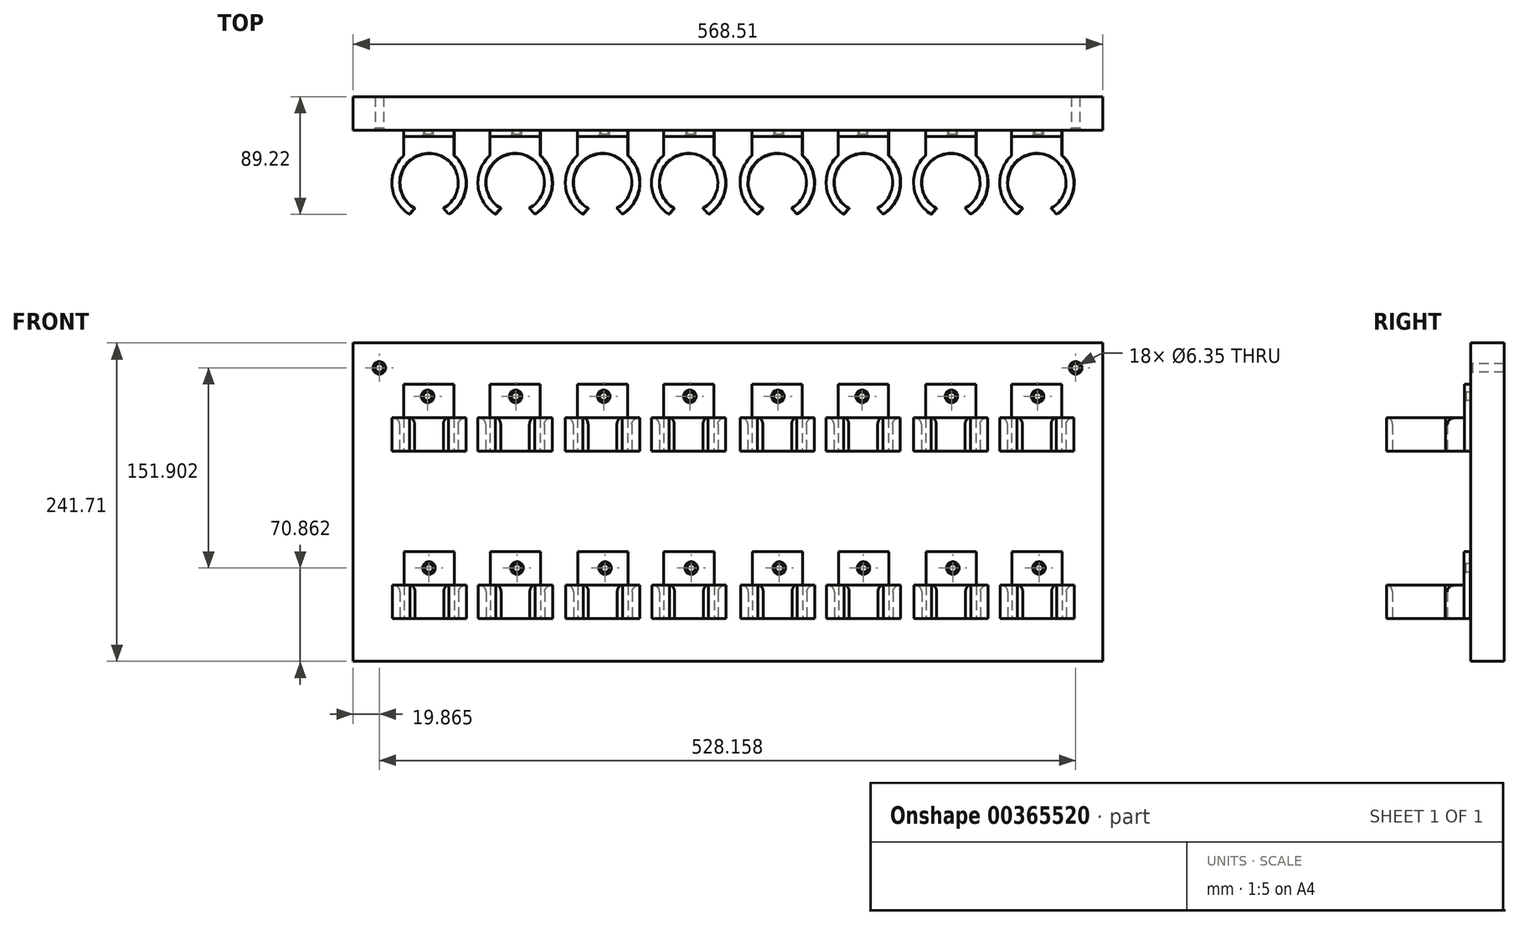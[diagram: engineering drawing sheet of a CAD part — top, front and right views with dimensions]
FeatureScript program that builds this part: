
annotation { "Feature Type Name" : "Feature", "Feature Type Description" : "" }
export const myFeature = defineFeature(function(context is Context, id is Id, definition is map)
    precondition{}
    {
        {
            var Q0;
            Q0=qCreatedBy(makeId("Top.planeOp"),FACE);
            var sketch = newSketch(context, id + "F0", { "sketchPlane" : qUnion([Q0])});
            skLineSegment(sketch, "E0.bottom", {"start": v(-209.16, -7.42) * mm, "end": v(-171.02, -7.42) * mm});
            skLineSegment(sketch, "E0.left", {"start": v(-209.16, -7.42) * mm, "end": v(-209.16, -26.47) * mm});
            skLineSegment(sketch, "E0.right", {"start": v(-171.02, -7.42) * mm, "end": v(-171.02, -26.47) * mm});
            skArc(sketch, "E1", {"start": v(-209.16, -26.47) * mm, "mid": v(-218.1, -49.8) * mm, "end": v(-204.97, -71.04) * mm});
            skArc(sketch, "E2", {"start": v(-175.21, -71.04) * mm, "mid": v(-190.1, -19.02) * mm, "end": v(-204.97, -71.04) * mm});
            skArc(sketch, "E3", {"start": v(-179.16, -66.5) * mm, "mid": v(-190.1, -24.93) * mm, "end": v(-201.02, -66.5) * mm});
            skPoint(sketch, "E4", {"position": v(-201.02, -66.5) * mm});
            skPoint(sketch, "E5", {"position": v(-204.97, -71.04) * mm});
            skPoint(sketch, "E6.MirrorP", {"position": v(-179.16, -66.5) * mm});
            skPoint(sketch, "E7.MirrorP", {"position": v(-175.21, -71.04) * mm});
            skArc(sketch, "E8.trimOffspring", {"start": v(-175.21, -71.04) * mm, "mid": v(-162.08, -49.8) * mm, "end": v(-171.02, -26.47) * mm});
            skPoint(sketch, "E9.orphan", {"position": v(-190.1, -7.42) * mm});
            skLineSegment(sketch, "E10", {"start": v(-201.02, -66.5) * mm, "end": v(-204.97, -71.04) * mm});
            skLineSegment(sketch, "E11", {"start": v(-179.16, -66.5) * mm, "end": v(-175.21, -71.04) * mm});
            skLineSegment(sketch, "E12.left", {"start": v(-209.16, -7.42) * mm, "end": v(-209.16, -16.94) * mm});
            skLineSegment(sketch, "E12.right", {"start": v(-171.02, -7.42) * mm, "end": v(-171.02, -16.94) * mm});
            skPoint(sketch, "E13.end.orphan", {"position": v(-209.16, -12.18) * mm});
            skPoint(sketch, "E13.start.orphan", {"position": v(-171.02, -12.18) * mm});
            skLineSegment(sketch, "E14.bottom", {"start": v(-209.16, -12.18) * mm, "end": v(-171.02, -12.18) * mm});
            skLineSegment(sketch, "E14.left", {"start": v(-209.16, -12.18) * mm, "end": v(-209.16, -7.42) * mm});
            skLineSegment(sketch, "E14.right", {"start": v(-171.02, -12.18) * mm, "end": v(-171.02, -7.42) * mm});
            skPoint(sketch, "E14.top.end.orphan", {"position": v(-171.02, -2.68) * mm});
            skLineSegment(sketch, "E15.bottom", {"start": v(-274.44, -7.42) * mm, "end": v(-236.3, -7.42) * mm});
            skLineSegment(sketch, "E15.left", {"start": v(-274.44, -7.42) * mm, "end": v(-274.44, -26.47) * mm});
            skLineSegment(sketch, "E15.right", {"start": v(-236.3, -7.42) * mm, "end": v(-236.3, -26.47) * mm});
            skArc(sketch, "E16", {"start": v(-274.44, -26.47) * mm, "mid": v(-283.38, -49.8) * mm, "end": v(-270.25, -71.04) * mm});
            skArc(sketch, "E17", {"start": v(-240.5, -71.04) * mm, "mid": v(-255.37, -19.02) * mm, "end": v(-270.25, -71.04) * mm});
            skArc(sketch, "E18", {"start": v(-244.44, -66.5) * mm, "mid": v(-255.37, -24.93) * mm, "end": v(-266.3, -66.5) * mm});
            skPoint(sketch, "E19", {"position": v(-266.3, -66.5) * mm});
            skPoint(sketch, "E20", {"position": v(-270.25, -71.04) * mm});
            skPoint(sketch, "E21.MirrorP", {"position": v(-244.44, -66.5) * mm});
            skPoint(sketch, "E22.MirrorP", {"position": v(-240.5, -71.04) * mm});
            skArc(sketch, "E23.trimOffspring", {"start": v(-240.5, -71.04) * mm, "mid": v(-227.36, -49.8) * mm, "end": v(-236.3, -26.47) * mm});
            skPoint(sketch, "E24.orphan", {"position": v(-255.37, -7.42) * mm});
            skLineSegment(sketch, "E25", {"start": v(-266.3, -66.5) * mm, "end": v(-270.25, -71.04) * mm});
            skLineSegment(sketch, "E26", {"start": v(-244.44, -66.5) * mm, "end": v(-240.5, -71.04) * mm});
            skLineSegment(sketch, "E27.left", {"start": v(-274.44, -7.42) * mm, "end": v(-274.44, -16.94) * mm});
            skLineSegment(sketch, "E27.right", {"start": v(-236.3, -7.42) * mm, "end": v(-236.3, -16.94) * mm});
            skPoint(sketch, "E28.end.orphan", {"position": v(-274.44, -12.18) * mm});
            skPoint(sketch, "E28.start.orphan", {"position": v(-236.3, -12.18) * mm});
            skLineSegment(sketch, "E29.bottom", {"start": v(-274.44, -12.18) * mm, "end": v(-236.3, -12.18) * mm});
            skLineSegment(sketch, "E29.left", {"start": v(-274.44, -12.18) * mm, "end": v(-274.44, -7.42) * mm});
            skLineSegment(sketch, "E29.right", {"start": v(-236.3, -12.18) * mm, "end": v(-236.3, -7.42) * mm});
            skPoint(sketch, "E29.top.end.orphan", {"position": v(-236.3, -2.68) * mm});
            skLineSegment(sketch, "E30.bottom", {"start": v(-77.55, -7.42) * mm, "end": v(-39.41, -7.42) * mm});
            skLineSegment(sketch, "E30.left", {"start": v(-77.55, -7.42) * mm, "end": v(-77.55, -26.47) * mm});
            skLineSegment(sketch, "E30.right", {"start": v(-39.41, -7.42) * mm, "end": v(-39.41, -26.47) * mm});
            skArc(sketch, "E31", {"start": v(-77.55, -26.47) * mm, "mid": v(-86.5, -49.8) * mm, "end": v(-73.36, -71.04) * mm});
            skArc(sketch, "E32", {"start": v(-43.6, -71.04) * mm, "mid": v(-58.48, -19.02) * mm, "end": v(-73.36, -71.04) * mm});
            skArc(sketch, "E33", {"start": v(-47.56, -66.5) * mm, "mid": v(-58.48, -24.93) * mm, "end": v(-69.41, -66.5) * mm});
            skPoint(sketch, "E34", {"position": v(-69.41, -66.5) * mm});
            skPoint(sketch, "E35", {"position": v(-73.36, -71.04) * mm});
            skPoint(sketch, "E36.MirrorP", {"position": v(-47.56, -66.5) * mm});
            skPoint(sketch, "E37.MirrorP", {"position": v(-43.6, -71.04) * mm});
            skArc(sketch, "E38.trimOffspring", {"start": v(-43.6, -71.04) * mm, "mid": v(-30.47, -49.8) * mm, "end": v(-39.41, -26.47) * mm});
            skPoint(sketch, "E39.orphan", {"position": v(-58.48, -7.42) * mm});
            skLineSegment(sketch, "E40", {"start": v(-69.41, -66.5) * mm, "end": v(-73.36, -71.04) * mm});
            skLineSegment(sketch, "E41", {"start": v(-47.56, -66.5) * mm, "end": v(-43.6, -71.04) * mm});
            skLineSegment(sketch, "E42.left", {"start": v(-77.55, -7.42) * mm, "end": v(-77.55, -16.94) * mm});
            skLineSegment(sketch, "E42.right", {"start": v(-39.41, -7.42) * mm, "end": v(-39.41, -16.94) * mm});
            skPoint(sketch, "E43.end.orphan", {"position": v(-77.55, -12.18) * mm});
            skPoint(sketch, "E43.start.orphan", {"position": v(-39.41, -12.18) * mm});
            skLineSegment(sketch, "E44.bottom", {"start": v(-77.55, -12.18) * mm, "end": v(-39.41, -12.18) * mm});
            skLineSegment(sketch, "E44.left", {"start": v(-77.55, -12.18) * mm, "end": v(-77.55, -7.42) * mm});
            skLineSegment(sketch, "E44.right", {"start": v(-39.41, -12.18) * mm, "end": v(-39.41, -7.42) * mm});
            skLineSegment(sketch, "E45.bottom", {"start": v(-142.83, -7.42) * mm, "end": v(-104.7, -7.42) * mm});
            skLineSegment(sketch, "E45.left", {"start": v(-142.83, -7.42) * mm, "end": v(-142.83, -26.47) * mm});
            skLineSegment(sketch, "E45.right", {"start": v(-104.7, -7.42) * mm, "end": v(-104.7, -26.47) * mm});
            skArc(sketch, "E46", {"start": v(-142.83, -26.47) * mm, "mid": v(-151.77, -49.8) * mm, "end": v(-138.64, -71.04) * mm});
            skArc(sketch, "E47", {"start": v(-108.88, -71.04) * mm, "mid": v(-123.76, -19.02) * mm, "end": v(-138.64, -71.04) * mm});
            skArc(sketch, "E48", {"start": v(-112.83, -66.5) * mm, "mid": v(-123.76, -24.93) * mm, "end": v(-134.69, -66.5) * mm});
            skPoint(sketch, "E49", {"position": v(-134.69, -66.5) * mm});
            skPoint(sketch, "E50", {"position": v(-138.64, -71.04) * mm});
            skPoint(sketch, "E51.MirrorP", {"position": v(-112.83, -66.5) * mm});
            skPoint(sketch, "E52.MirrorP", {"position": v(-108.88, -71.04) * mm});
            skArc(sketch, "E53.trimOffspring", {"start": v(-108.88, -71.04) * mm, "mid": v(-95.75, -49.8) * mm, "end": v(-104.7, -26.47) * mm});
            skPoint(sketch, "E54.orphan", {"position": v(-123.76, -7.42) * mm});
            skLineSegment(sketch, "E55", {"start": v(-134.69, -66.5) * mm, "end": v(-138.64, -71.04) * mm});
            skLineSegment(sketch, "E56", {"start": v(-112.83, -66.5) * mm, "end": v(-108.88, -71.04) * mm});
            skLineSegment(sketch, "E57.left", {"start": v(-142.83, -7.42) * mm, "end": v(-142.83, -16.94) * mm});
            skLineSegment(sketch, "E57.right", {"start": v(-104.7, -7.42) * mm, "end": v(-104.7, -16.94) * mm});
            skPoint(sketch, "E58.end.orphan", {"position": v(-142.83, -12.18) * mm});
            skPoint(sketch, "E58.start.orphan", {"position": v(-104.7, -12.18) * mm});
            skLineSegment(sketch, "E59.bottom", {"start": v(-142.83, -12.18) * mm, "end": v(-104.7, -12.18) * mm});
            skLineSegment(sketch, "E59.left", {"start": v(-142.83, -12.18) * mm, "end": v(-142.83, -7.42) * mm});
            skLineSegment(sketch, "E59.right", {"start": v(-104.7, -12.18) * mm, "end": v(-104.7, -7.42) * mm});
            skLineSegment(sketch, "E60.bottom", {"start": v(54.94, -7.42) * mm, "end": v(93.08, -7.42) * mm});
            skLineSegment(sketch, "E60.left", {"start": v(54.94, -7.42) * mm, "end": v(54.94, -26.47) * mm});
            skLineSegment(sketch, "E60.right", {"start": v(93.08, -7.42) * mm, "end": v(93.08, -26.47) * mm});
            skArc(sketch, "E61", {"start": v(54.94, -26.47) * mm, "mid": v(46, -49.8) * mm, "end": v(59.14, -71.04) * mm});
            skArc(sketch, "E62", {"start": v(88.89, -71.04) * mm, "mid": v(74.01, -19.02) * mm, "end": v(59.14, -71.04) * mm});
            skArc(sketch, "E63", {"start": v(84.94, -66.5) * mm, "mid": v(74.01, -24.93) * mm, "end": v(63.09, -66.5) * mm});
            skPoint(sketch, "E64", {"position": v(63.09, -66.5) * mm});
            skPoint(sketch, "E65", {"position": v(59.14, -71.04) * mm});
            skPoint(sketch, "E66.MirrorP", {"position": v(84.94, -66.5) * mm});
            skPoint(sketch, "E67.MirrorP", {"position": v(88.89, -71.04) * mm});
            skArc(sketch, "E68.trimOffspring", {"start": v(88.89, -71.04) * mm, "mid": v(102.03, -49.8) * mm, "end": v(93.08, -26.47) * mm});
            skPoint(sketch, "E69.orphan", {"position": v(74.01, -7.42) * mm});
            skLineSegment(sketch, "E70", {"start": v(63.09, -66.5) * mm, "end": v(59.14, -71.04) * mm});
            skLineSegment(sketch, "E71", {"start": v(84.94, -66.5) * mm, "end": v(88.89, -71.04) * mm});
            skLineSegment(sketch, "E72.left", {"start": v(54.94, -7.42) * mm, "end": v(54.94, -16.94) * mm});
            skLineSegment(sketch, "E72.right", {"start": v(93.08, -7.42) * mm, "end": v(93.08, -16.94) * mm});
            skPoint(sketch, "E73.end.orphan", {"position": v(54.94, -12.18) * mm});
            skPoint(sketch, "E73.start.orphan", {"position": v(93.08, -12.18) * mm});
            skLineSegment(sketch, "E74.bottom", {"start": v(54.94, -12.18) * mm, "end": v(93.08, -12.18) * mm});
            skLineSegment(sketch, "E74.left", {"start": v(54.94, -12.18) * mm, "end": v(54.94, -7.42) * mm});
            skLineSegment(sketch, "E74.right", {"start": v(93.08, -12.18) * mm, "end": v(93.08, -7.42) * mm});
            skPoint(sketch, "E74.top.end.orphan", {"position": v(93.08, -2.68) * mm});
            skLineSegment(sketch, "E75.bottom", {"start": v(-10.34, -7.42) * mm, "end": v(27.8, -7.42) * mm});
            skLineSegment(sketch, "E75.left", {"start": v(-10.34, -7.42) * mm, "end": v(-10.34, -26.47) * mm});
            skLineSegment(sketch, "E75.right", {"start": v(27.8, -7.42) * mm, "end": v(27.8, -26.47) * mm});
            skArc(sketch, "E76", {"start": v(-10.34, -26.47) * mm, "mid": v(-19.28, -49.8) * mm, "end": v(-6.14, -71.04) * mm});
            skArc(sketch, "E77", {"start": v(23.61, -71.04) * mm, "mid": v(8.73, -19.02) * mm, "end": v(-6.14, -71.04) * mm});
            skArc(sketch, "E78", {"start": v(19.66, -66.5) * mm, "mid": v(8.73, -24.93) * mm, "end": v(-2.2, -66.5) * mm});
            skPoint(sketch, "E79", {"position": v(-2.2, -66.5) * mm});
            skPoint(sketch, "E80", {"position": v(-6.14, -71.04) * mm});
            skPoint(sketch, "E81.MirrorP", {"position": v(19.66, -66.5) * mm});
            skPoint(sketch, "E82.MirrorP", {"position": v(23.61, -71.04) * mm});
            skArc(sketch, "E83.trimOffspring", {"start": v(23.61, -71.04) * mm, "mid": v(36.75, -49.8) * mm, "end": v(27.8, -26.47) * mm});
            skPoint(sketch, "E84.orphan", {"position": v(8.73, -7.42) * mm});
            skLineSegment(sketch, "E85", {"start": v(-2.2, -66.5) * mm, "end": v(-6.14, -71.04) * mm});
            skLineSegment(sketch, "E86", {"start": v(19.66, -66.5) * mm, "end": v(23.61, -71.04) * mm});
            skLineSegment(sketch, "E87.left", {"start": v(-10.34, -7.42) * mm, "end": v(-10.34, -16.94) * mm});
            skLineSegment(sketch, "E87.right", {"start": v(27.8, -7.42) * mm, "end": v(27.8, -16.94) * mm});
            skPoint(sketch, "E88.end.orphan", {"position": v(-10.34, -12.18) * mm});
            skPoint(sketch, "E88.start.orphan", {"position": v(27.8, -12.18) * mm});
            skLineSegment(sketch, "E89.bottom", {"start": v(-10.34, -12.18) * mm, "end": v(27.8, -12.18) * mm});
            skLineSegment(sketch, "E89.left", {"start": v(-10.34, -12.18) * mm, "end": v(-10.34, -7.42) * mm});
            skLineSegment(sketch, "E89.right", {"start": v(27.8, -12.18) * mm, "end": v(27.8, -7.42) * mm});
            skPoint(sketch, "E89.top.end.orphan", {"position": v(27.8, -2.68) * mm});
            skLineSegment(sketch, "E90.bottom", {"start": v(186.55, -7.42) * mm, "end": v(224.7, -7.42) * mm});
            skLineSegment(sketch, "E90.left", {"start": v(186.55, -7.42) * mm, "end": v(186.55, -26.47) * mm});
            skLineSegment(sketch, "E90.right", {"start": v(224.7, -7.42) * mm, "end": v(224.7, -26.47) * mm});
            skArc(sketch, "E91", {"start": v(186.55, -26.47) * mm, "mid": v(177.6, -49.8) * mm, "end": v(190.74, -71.04) * mm});
            skArc(sketch, "E92", {"start": v(220.5, -71.04) * mm, "mid": v(205.62, -19.02) * mm, "end": v(190.74, -71.04) * mm});
            skArc(sketch, "E93", {"start": v(216.55, -66.5) * mm, "mid": v(205.62, -24.93) * mm, "end": v(194.7, -66.5) * mm});
            skPoint(sketch, "E94", {"position": v(194.7, -66.5) * mm});
            skPoint(sketch, "E95", {"position": v(190.74, -71.04) * mm});
            skPoint(sketch, "E96.MirrorP", {"position": v(216.55, -66.5) * mm});
            skPoint(sketch, "E97.MirrorP", {"position": v(220.5, -71.04) * mm});
            skArc(sketch, "E98.trimOffspring", {"start": v(220.5, -71.04) * mm, "mid": v(233.63, -49.8) * mm, "end": v(224.7, -26.47) * mm});
            skPoint(sketch, "E99.orphan", {"position": v(205.62, -7.42) * mm});
            skLineSegment(sketch, "E100", {"start": v(194.7, -66.5) * mm, "end": v(190.74, -71.04) * mm});
            skLineSegment(sketch, "E101", {"start": v(216.55, -66.5) * mm, "end": v(220.5, -71.04) * mm});
            skLineSegment(sketch, "E102.left", {"start": v(186.55, -7.42) * mm, "end": v(186.55, -16.94) * mm});
            skLineSegment(sketch, "E102.right", {"start": v(224.7, -7.42) * mm, "end": v(224.7, -16.94) * mm});
            skPoint(sketch, "E103.end.orphan", {"position": v(186.55, -12.18) * mm});
            skPoint(sketch, "E103.start.orphan", {"position": v(224.7, -12.18) * mm});
            skLineSegment(sketch, "E104.bottom", {"start": v(186.55, -12.18) * mm, "end": v(224.7, -12.18) * mm});
            skLineSegment(sketch, "E104.left", {"start": v(186.55, -12.18) * mm, "end": v(186.55, -7.42) * mm});
            skLineSegment(sketch, "E104.right", {"start": v(224.7, -12.18) * mm, "end": v(224.7, -7.42) * mm});
            skLineSegment(sketch, "E105.bottom", {"start": v(121.27, -7.42) * mm, "end": v(159.41, -7.42) * mm});
            skLineSegment(sketch, "E105.left", {"start": v(121.27, -7.42) * mm, "end": v(121.27, -26.47) * mm});
            skLineSegment(sketch, "E105.right", {"start": v(159.41, -7.42) * mm, "end": v(159.41, -26.47) * mm});
            skArc(sketch, "E106", {"start": v(121.27, -26.47) * mm, "mid": v(112.33, -49.8) * mm, "end": v(125.47, -71.04) * mm});
            skArc(sketch, "E107", {"start": v(155.22, -71.04) * mm, "mid": v(140.34, -19.02) * mm, "end": v(125.47, -71.04) * mm});
            skArc(sketch, "E108", {"start": v(151.27, -66.5) * mm, "mid": v(140.34, -24.93) * mm, "end": v(129.42, -66.5) * mm});
            skPoint(sketch, "E109", {"position": v(129.42, -66.5) * mm});
            skPoint(sketch, "E110", {"position": v(125.47, -71.04) * mm});
            skPoint(sketch, "E111.MirrorP", {"position": v(151.27, -66.5) * mm});
            skPoint(sketch, "E112.MirrorP", {"position": v(155.22, -71.04) * mm});
            skArc(sketch, "E113.trimOffspring", {"start": v(155.22, -71.04) * mm, "mid": v(168.36, -49.8) * mm, "end": v(159.41, -26.47) * mm});
            skPoint(sketch, "E114.orphan", {"position": v(140.34, -7.42) * mm});
            skLineSegment(sketch, "E115", {"start": v(129.42, -66.5) * mm, "end": v(125.47, -71.04) * mm});
            skLineSegment(sketch, "E116", {"start": v(151.27, -66.5) * mm, "end": v(155.22, -71.04) * mm});
            skLineSegment(sketch, "E117.left", {"start": v(121.27, -7.42) * mm, "end": v(121.27, -16.94) * mm});
            skLineSegment(sketch, "E117.right", {"start": v(159.41, -7.42) * mm, "end": v(159.41, -16.94) * mm});
            skPoint(sketch, "E118.end.orphan", {"position": v(121.27, -12.18) * mm});
            skPoint(sketch, "E118.start.orphan", {"position": v(159.41, -12.18) * mm});
            skLineSegment(sketch, "E119.bottom", {"start": v(121.27, -12.18) * mm, "end": v(159.41, -12.18) * mm});
            skLineSegment(sketch, "E119.left", {"start": v(121.27, -12.18) * mm, "end": v(121.27, -7.42) * mm});
            skLineSegment(sketch, "E119.right", {"start": v(159.41, -12.18) * mm, "end": v(159.41, -7.42) * mm});
            skSolve(sketch);
        }
        {
            var Q0;
            {var subQ1=sQuery(id+"F0.wireOp",EDGE,"E15.left");Q0=makeQuery(id+"F0.imprint","IMPRINT",FACE,{"disambiguationData":[TD([[makeQuery(id+"F0.imprint","IMPRINT",EDGE,{"derivedFrom":subQ1}),1.0]])]});}
            var Q1;
            Q1=makeQuery(id+"F0.imprint","IMPRINT",FACE,{"disambiguationData":[TD([[makeQuery(id+"F0.imprint","IMPRINT",EDGE,{"derivedFrom":sQuery(id+"F0.wireOp",EDGE,"E18")}),-1.0]])]});
            var Q2;
            Q2=makeQuery(id+"F0.imprint","IMPRINT",FACE,{"disambiguationData":[TD([[makeQuery(id+"F0.imprint","IMPRINT",EDGE,{"derivedFrom":sQuery(id+"F0.wireOp",EDGE,"E3")}),-1.0]])]});
            var Q3;
            {var subQ1=sQuery(id+"F0.wireOp",EDGE,"E0.left");Q3=makeQuery(id+"F0.imprint","IMPRINT",FACE,{"disambiguationData":[TD([[makeQuery(id+"F0.imprint","IMPRINT",EDGE,{"derivedFrom":subQ1}),1.0]])]});}
            var Q4;
            {var subQ1=sQuery(id+"F0.wireOp",EDGE,"E45.left");Q4=makeQuery(id+"F0.imprint","IMPRINT",FACE,{"disambiguationData":[TD([[makeQuery(id+"F0.imprint","IMPRINT",EDGE,{"derivedFrom":subQ1}),1.0]])]});}
            var Q5;
            Q5=makeQuery(id+"F0.imprint","IMPRINT",FACE,{"disambiguationData":[TD([[makeQuery(id+"F0.imprint","IMPRINT",EDGE,{"derivedFrom":sQuery(id+"F0.wireOp",EDGE,"E48")}),-1.0]])]});
            var Q6;
            Q6=makeQuery(id+"F0.imprint","IMPRINT",FACE,{"disambiguationData":[TD([[makeQuery(id+"F0.imprint","IMPRINT",EDGE,{"derivedFrom":sQuery(id+"F0.wireOp",EDGE,"E33")}),-1.0]])]});
            var Q7;
            Q7=makeQuery(id+"F0.imprint","IMPRINT",FACE,{"disambiguationData":[TD([[makeQuery(id+"F0.imprint","IMPRINT",EDGE,{"derivedFrom":sQuery(id+"F0.wireOp",EDGE,"E78")}),-1.0]])]});
            var Q8;
            Q8=makeQuery(id+"F0.imprint","IMPRINT",FACE,{"disambiguationData":[TD([[makeQuery(id+"F0.imprint","IMPRINT",EDGE,{"derivedFrom":sQuery(id+"F0.wireOp",EDGE,"E63")}),-1.0]])]});
            var Q9;
            Q9=makeQuery(id+"F0.imprint","IMPRINT",FACE,{"disambiguationData":[TD([[makeQuery(id+"F0.imprint","IMPRINT",EDGE,{"derivedFrom":sQuery(id+"F0.wireOp",EDGE,"E108")}),-1.0]])]});
            var Q10;
            Q10=makeQuery(id+"F0.imprint","IMPRINT",FACE,{"disambiguationData":[TD([[makeQuery(id+"F0.imprint","IMPRINT",EDGE,{"derivedFrom":sQuery(id+"F0.wireOp",EDGE,"E93")}),-1.0]])]});
            var Q11;
            {var subQ1=sQuery(id+"F0.wireOp",EDGE,"E105.left");Q11=makeQuery(id+"F0.imprint","IMPRINT",FACE,{"disambiguationData":[TD([[makeQuery(id+"F0.imprint","IMPRINT",EDGE,{"derivedFrom":subQ1}),1.0]])]});}
            var Q12;
            {var subQ1=sQuery(id+"F0.wireOp",EDGE,"E60.left");Q12=makeQuery(id+"F0.imprint","IMPRINT",FACE,{"disambiguationData":[TD([[makeQuery(id+"F0.imprint","IMPRINT",EDGE,{"derivedFrom":subQ1}),1.0]])]});}
            var Q13;
            {var subQ1=sQuery(id+"F0.wireOp",EDGE,"E75.left");Q13=makeQuery(id+"F0.imprint","IMPRINT",FACE,{"disambiguationData":[TD([[makeQuery(id+"F0.imprint","IMPRINT",EDGE,{"derivedFrom":subQ1}),1.0]])]});}
            var Q14;
            {var subQ1=sQuery(id+"F0.wireOp",EDGE,"E30.left");Q14=makeQuery(id+"F0.imprint","IMPRINT",FACE,{"disambiguationData":[TD([[makeQuery(id+"F0.imprint","IMPRINT",EDGE,{"derivedFrom":subQ1}),1.0]])]});}
            var Q15;
            {var subQ1=sQuery(id+"F0.wireOp",EDGE,"E90.left");Q15=makeQuery(id+"F0.imprint","IMPRINT",FACE,{"disambiguationData":[TD([[makeQuery(id+"F0.imprint","IMPRINT",EDGE,{"derivedFrom":subQ1}),1.0]])]});}
            var Q16;
            Q16=makeQuery(id+"F0.imprint","IMPRINT",FACE,{"disambiguationData":[TD([[makeQuery(id+"F0.imprint","IMPRINT",EDGE,{"derivedFrom":sQuery(id+"F0.wireOp",EDGE,"c035edba-2ca9-43be-b41b-8822a2fe950e")}),-1.0]])]});
            var Q17;
            {var subQ1=sQuery(id+"F0.wireOp",EDGE,"01a7d978-39eb-4d9a-a90e-11414904825e.left");Q17=makeQuery(id+"F0.imprint","IMPRINT",FACE,{"disambiguationData":[TD([[makeQuery(id+"F0.imprint","IMPRINT",EDGE,{"derivedFrom":subQ1}),1.0]])]});}
            extrude(context, id + "F1", {"entities" : qUnion([Q0, Q1, Q2, Q3, Q4, Q5, Q6, Q7, Q8, Q9, Q10, Q11, Q12, Q13, Q14, Q15, Q16, Q17]), "depth" : 25.4 * mm});
        }
        {
            var Q0;
            Q0=qCreatedBy(makeId("Top.planeOp"),FACE);
            cPlane(context, id + "F2", {"entities" : qUnion([Q0]), "cplaneType" : CPlaneType.OFFSET, "offset" : 127 * mm, "oppositeDirection" : true, "width" : 152.4 * mm, "height" : 152.4 * mm});
        }
        {
            var Q0;
            Q0=qCreatedBy(id+"F2.planeOp",FACE);
            var sketch = newSketch(context, id + "F3", { "sketchPlane" : qUnion([Q0])});
            skLineSegment(sketch, "E120.bottom", {"start": v(-208.88, -7.62) * mm, "end": v(-170.73, -7.62) * mm});
            skLineSegment(sketch, "E120.left", {"start": v(-208.88, -7.62) * mm, "end": v(-208.88, -26.67) * mm});
            skLineSegment(sketch, "E120.right", {"start": v(-170.73, -7.62) * mm, "end": v(-170.73, -26.67) * mm});
            skArc(sketch, "E121", {"start": v(-208.88, -26.67) * mm, "mid": v(-217.82, -50) * mm, "end": v(-204.68, -71.24) * mm});
            skArc(sketch, "E122", {"start": v(-174.93, -71.24) * mm, "mid": v(-189.8, -19.22) * mm, "end": v(-204.68, -71.24) * mm});
            skArc(sketch, "E123", {"start": v(-178.88, -66.7) * mm, "mid": v(-189.8, -25.13) * mm, "end": v(-200.73, -66.7) * mm});
            skPoint(sketch, "E124", {"position": v(-200.73, -66.7) * mm});
            skPoint(sketch, "E125", {"position": v(-204.68, -71.24) * mm});
            skPoint(sketch, "E126.MirrorP", {"position": v(-178.88, -66.7) * mm});
            skPoint(sketch, "E127.MirrorP", {"position": v(-174.93, -71.24) * mm});
            skArc(sketch, "E128.trimOffspring", {"start": v(-174.93, -71.24) * mm, "mid": v(-161.8, -50) * mm, "end": v(-170.73, -26.67) * mm});
            skPoint(sketch, "E129.orphan", {"position": v(-189.8, -7.62) * mm});
            skLineSegment(sketch, "E130", {"start": v(-200.73, -66.7) * mm, "end": v(-204.68, -71.24) * mm});
            skLineSegment(sketch, "E131", {"start": v(-178.88, -66.7) * mm, "end": v(-174.93, -71.24) * mm});
            skLineSegment(sketch, "E132.left", {"start": v(-208.88, -7.62) * mm, "end": v(-208.88, -17.14) * mm});
            skLineSegment(sketch, "E132.right", {"start": v(-170.73, -7.62) * mm, "end": v(-170.73, -17.14) * mm});
            skPoint(sketch, "E133.end.orphan", {"position": v(-208.88, -12.38) * mm});
            skPoint(sketch, "E133.start.orphan", {"position": v(-170.73, -12.38) * mm});
            skLineSegment(sketch, "E134.bottom", {"start": v(-208.88, -12.38) * mm, "end": v(-170.73, -12.38) * mm});
            skLineSegment(sketch, "E134.left", {"start": v(-208.88, -12.38) * mm, "end": v(-208.88, -7.62) * mm});
            skLineSegment(sketch, "E134.right", {"start": v(-170.73, -12.38) * mm, "end": v(-170.73, -7.62) * mm});
            skPoint(sketch, "E134.top.end.orphan", {"position": v(-170.73, -2.88) * mm});
            skLineSegment(sketch, "E135.bottom", {"start": v(-274.15, -7.62) * mm, "end": v(-236.01, -7.62) * mm});
            skLineSegment(sketch, "E135.left", {"start": v(-274.15, -7.62) * mm, "end": v(-274.15, -26.67) * mm});
            skLineSegment(sketch, "E135.right", {"start": v(-236.01, -7.62) * mm, "end": v(-236.01, -26.67) * mm});
            skArc(sketch, "E136", {"start": v(-274.15, -26.67) * mm, "mid": v(-283.1, -50) * mm, "end": v(-269.96, -71.24) * mm});
            skArc(sketch, "E137", {"start": v(-240.2, -71.24) * mm, "mid": v(-255.08, -19.22) * mm, "end": v(-269.96, -71.24) * mm});
            skArc(sketch, "E138", {"start": v(-244.16, -66.7) * mm, "mid": v(-255.08, -25.13) * mm, "end": v(-266.01, -66.7) * mm});
            skPoint(sketch, "E139", {"position": v(-266.01, -66.7) * mm});
            skPoint(sketch, "E140", {"position": v(-269.96, -71.24) * mm});
            skPoint(sketch, "E141.MirrorP", {"position": v(-244.16, -66.7) * mm});
            skPoint(sketch, "E142.MirrorP", {"position": v(-240.2, -71.24) * mm});
            skArc(sketch, "E143.trimOffspring", {"start": v(-240.2, -71.24) * mm, "mid": v(-227.07, -50) * mm, "end": v(-236.01, -26.67) * mm});
            skPoint(sketch, "E144.orphan", {"position": v(-255.08, -7.62) * mm});
            skLineSegment(sketch, "E145", {"start": v(-266.01, -66.7) * mm, "end": v(-269.96, -71.24) * mm});
            skLineSegment(sketch, "E146", {"start": v(-244.16, -66.7) * mm, "end": v(-240.2, -71.24) * mm});
            skLineSegment(sketch, "E147.left", {"start": v(-274.15, -7.62) * mm, "end": v(-274.15, -17.14) * mm});
            skLineSegment(sketch, "E147.right", {"start": v(-236.01, -7.62) * mm, "end": v(-236.01, -17.14) * mm});
            skPoint(sketch, "E148.end.orphan", {"position": v(-274.15, -12.38) * mm});
            skPoint(sketch, "E148.start.orphan", {"position": v(-236.01, -12.38) * mm});
            skLineSegment(sketch, "E149.bottom", {"start": v(-274.15, -12.38) * mm, "end": v(-236.01, -12.38) * mm});
            skLineSegment(sketch, "E149.left", {"start": v(-274.15, -12.38) * mm, "end": v(-274.15, -7.62) * mm});
            skLineSegment(sketch, "E149.right", {"start": v(-236.01, -12.38) * mm, "end": v(-236.01, -7.62) * mm});
            skPoint(sketch, "E149.top.end.orphan", {"position": v(-236.01, -2.88) * mm});
            skLineSegment(sketch, "E150.bottom", {"start": v(-77.27, -7.62) * mm, "end": v(-39.13, -7.62) * mm});
            skLineSegment(sketch, "E150.left", {"start": v(-77.27, -7.62) * mm, "end": v(-77.27, -26.67) * mm});
            skLineSegment(sketch, "E150.right", {"start": v(-39.13, -7.62) * mm, "end": v(-39.13, -26.67) * mm});
            skArc(sketch, "E151", {"start": v(-77.27, -26.67) * mm, "mid": v(-86.21, -50) * mm, "end": v(-73.07, -71.24) * mm});
            skArc(sketch, "E152", {"start": v(-43.32, -71.24) * mm, "mid": v(-58.2, -19.22) * mm, "end": v(-73.07, -71.24) * mm});
            skArc(sketch, "E153", {"start": v(-47.27, -66.7) * mm, "mid": v(-58.2, -25.13) * mm, "end": v(-69.12, -66.7) * mm});
            skPoint(sketch, "E154", {"position": v(-69.12, -66.7) * mm});
            skPoint(sketch, "E155", {"position": v(-73.07, -71.24) * mm});
            skPoint(sketch, "E156.MirrorP", {"position": v(-47.27, -66.7) * mm});
            skPoint(sketch, "E157.MirrorP", {"position": v(-43.32, -71.24) * mm});
            skArc(sketch, "E158.trimOffspring", {"start": v(-43.32, -71.24) * mm, "mid": v(-30.18, -50) * mm, "end": v(-39.13, -26.67) * mm});
            skPoint(sketch, "E159.orphan", {"position": v(-58.2, -7.62) * mm});
            skLineSegment(sketch, "E160", {"start": v(-69.12, -66.7) * mm, "end": v(-73.07, -71.24) * mm});
            skLineSegment(sketch, "E161", {"start": v(-47.27, -66.7) * mm, "end": v(-43.32, -71.24) * mm});
            skLineSegment(sketch, "E162.left", {"start": v(-77.27, -7.62) * mm, "end": v(-77.27, -17.14) * mm});
            skLineSegment(sketch, "E162.right", {"start": v(-39.13, -7.62) * mm, "end": v(-39.13, -17.14) * mm});
            skPoint(sketch, "E163.end.orphan", {"position": v(-77.27, -12.38) * mm});
            skPoint(sketch, "E163.start.orphan", {"position": v(-39.13, -12.38) * mm});
            skLineSegment(sketch, "E164.bottom", {"start": v(-77.27, -12.38) * mm, "end": v(-39.13, -12.38) * mm});
            skLineSegment(sketch, "E164.left", {"start": v(-77.27, -12.38) * mm, "end": v(-77.27, -7.62) * mm});
            skLineSegment(sketch, "E164.right", {"start": v(-39.13, -12.38) * mm, "end": v(-39.13, -7.62) * mm});
            skLineSegment(sketch, "E165.bottom", {"start": v(-142.55, -7.62) * mm, "end": v(-104.4, -7.62) * mm});
            skLineSegment(sketch, "E165.left", {"start": v(-142.55, -7.62) * mm, "end": v(-142.55, -26.67) * mm});
            skLineSegment(sketch, "E165.right", {"start": v(-104.4, -7.62) * mm, "end": v(-104.4, -26.67) * mm});
            skArc(sketch, "E166", {"start": v(-142.55, -26.67) * mm, "mid": v(-151.49, -50) * mm, "end": v(-138.35, -71.24) * mm});
            skArc(sketch, "E167", {"start": v(-108.6, -71.24) * mm, "mid": v(-123.48, -19.22) * mm, "end": v(-138.35, -71.24) * mm});
            skArc(sketch, "E168", {"start": v(-112.55, -66.7) * mm, "mid": v(-123.48, -25.13) * mm, "end": v(-134.4, -66.7) * mm});
            skPoint(sketch, "E169", {"position": v(-134.4, -66.7) * mm});
            skPoint(sketch, "E170", {"position": v(-138.35, -71.24) * mm});
            skPoint(sketch, "E171.MirrorP", {"position": v(-112.55, -66.7) * mm});
            skPoint(sketch, "E172.MirrorP", {"position": v(-108.6, -71.24) * mm});
            skArc(sketch, "E173.trimOffspring", {"start": v(-108.6, -71.24) * mm, "mid": v(-95.46, -50) * mm, "end": v(-104.4, -26.67) * mm});
            skPoint(sketch, "E174.orphan", {"position": v(-123.48, -7.62) * mm});
            skLineSegment(sketch, "E175", {"start": v(-134.4, -66.7) * mm, "end": v(-138.35, -71.24) * mm});
            skLineSegment(sketch, "E176", {"start": v(-112.55, -66.7) * mm, "end": v(-108.6, -71.24) * mm});
            skLineSegment(sketch, "E177.left", {"start": v(-142.55, -7.62) * mm, "end": v(-142.55, -17.14) * mm});
            skLineSegment(sketch, "E177.right", {"start": v(-104.4, -7.62) * mm, "end": v(-104.4, -17.14) * mm});
            skPoint(sketch, "E178.end.orphan", {"position": v(-142.55, -12.38) * mm});
            skPoint(sketch, "E178.start.orphan", {"position": v(-104.4, -12.38) * mm});
            skLineSegment(sketch, "E179.bottom", {"start": v(-142.55, -12.38) * mm, "end": v(-104.4, -12.38) * mm});
            skLineSegment(sketch, "E179.left", {"start": v(-142.55, -12.38) * mm, "end": v(-142.55, -7.62) * mm});
            skLineSegment(sketch, "E179.right", {"start": v(-104.4, -12.38) * mm, "end": v(-104.4, -7.62) * mm});
            skLineSegment(sketch, "E180.bottom", {"start": v(55.23, -7.62) * mm, "end": v(93.37, -7.62) * mm});
            skLineSegment(sketch, "E180.left", {"start": v(55.23, -7.62) * mm, "end": v(55.23, -26.67) * mm});
            skLineSegment(sketch, "E180.right", {"start": v(93.37, -7.62) * mm, "end": v(93.37, -26.67) * mm});
            skArc(sketch, "E181", {"start": v(55.23, -26.67) * mm, "mid": v(46.29, -50) * mm, "end": v(59.42, -71.24) * mm});
            skArc(sketch, "E182", {"start": v(89.18, -71.24) * mm, "mid": v(74.3, -19.22) * mm, "end": v(59.42, -71.24) * mm});
            skArc(sketch, "E183", {"start": v(85.23, -66.7) * mm, "mid": v(74.3, -25.13) * mm, "end": v(63.37, -66.7) * mm});
            skPoint(sketch, "E184", {"position": v(63.37, -66.7) * mm});
            skPoint(sketch, "E185", {"position": v(59.42, -71.24) * mm});
            skPoint(sketch, "E186.MirrorP", {"position": v(85.23, -66.7) * mm});
            skPoint(sketch, "E187.MirrorP", {"position": v(89.18, -71.24) * mm});
            skArc(sketch, "E188.trimOffspring", {"start": v(89.18, -71.24) * mm, "mid": v(102.31, -50) * mm, "end": v(93.37, -26.67) * mm});
            skPoint(sketch, "E189.orphan", {"position": v(74.3, -7.62) * mm});
            skLineSegment(sketch, "E190", {"start": v(63.37, -66.7) * mm, "end": v(59.42, -71.24) * mm});
            skLineSegment(sketch, "E191", {"start": v(85.23, -66.7) * mm, "end": v(89.18, -71.24) * mm});
            skLineSegment(sketch, "E192.left", {"start": v(55.23, -7.62) * mm, "end": v(55.23, -17.14) * mm});
            skLineSegment(sketch, "E192.right", {"start": v(93.37, -7.62) * mm, "end": v(93.37, -17.14) * mm});
            skPoint(sketch, "E193.end.orphan", {"position": v(55.23, -12.38) * mm});
            skPoint(sketch, "E193.start.orphan", {"position": v(93.37, -12.38) * mm});
            skLineSegment(sketch, "E194.bottom", {"start": v(55.23, -12.38) * mm, "end": v(93.37, -12.38) * mm});
            skLineSegment(sketch, "E194.left", {"start": v(55.23, -12.38) * mm, "end": v(55.23, -7.62) * mm});
            skLineSegment(sketch, "E194.right", {"start": v(93.37, -12.38) * mm, "end": v(93.37, -7.62) * mm});
            skPoint(sketch, "E194.top.end.orphan", {"position": v(93.37, -2.88) * mm});
            skLineSegment(sketch, "E195.bottom", {"start": v(-10.05, -7.62) * mm, "end": v(28.1, -7.62) * mm});
            skLineSegment(sketch, "E195.left", {"start": v(-10.05, -7.62) * mm, "end": v(-10.05, -26.67) * mm});
            skLineSegment(sketch, "E195.right", {"start": v(28.1, -7.62) * mm, "end": v(28.1, -26.67) * mm});
            skArc(sketch, "E196", {"start": v(-10.05, -26.67) * mm, "mid": v(-19, -50) * mm, "end": v(-5.86, -71.24) * mm});
            skArc(sketch, "E197", {"start": v(23.9, -71.24) * mm, "mid": v(9.02, -19.22) * mm, "end": v(-5.86, -71.24) * mm});
            skArc(sketch, "E198", {"start": v(19.95, -66.7) * mm, "mid": v(9.02, -25.13) * mm, "end": v(-1.9, -66.7) * mm});
            skPoint(sketch, "E199", {"position": v(-1.9, -66.7) * mm});
            skPoint(sketch, "E200", {"position": v(-5.86, -71.24) * mm});
            skPoint(sketch, "E201.MirrorP", {"position": v(19.95, -66.7) * mm});
            skPoint(sketch, "E202.MirrorP", {"position": v(23.9, -71.24) * mm});
            skArc(sketch, "E203.trimOffspring", {"start": v(23.9, -71.24) * mm, "mid": v(37.03, -50) * mm, "end": v(28.1, -26.67) * mm});
            skPoint(sketch, "E204.orphan", {"position": v(9.02, -7.62) * mm});
            skLineSegment(sketch, "E205", {"start": v(-1.9, -66.7) * mm, "end": v(-5.86, -71.24) * mm});
            skLineSegment(sketch, "E206", {"start": v(19.95, -66.7) * mm, "end": v(23.9, -71.24) * mm});
            skLineSegment(sketch, "E207.left", {"start": v(-10.05, -7.62) * mm, "end": v(-10.05, -17.14) * mm});
            skLineSegment(sketch, "E207.right", {"start": v(28.1, -7.62) * mm, "end": v(28.1, -17.14) * mm});
            skPoint(sketch, "E208.end.orphan", {"position": v(-10.05, -12.38) * mm});
            skPoint(sketch, "E208.start.orphan", {"position": v(28.1, -12.38) * mm});
            skLineSegment(sketch, "E209.bottom", {"start": v(-10.05, -12.38) * mm, "end": v(28.1, -12.38) * mm});
            skLineSegment(sketch, "E209.left", {"start": v(-10.05, -12.38) * mm, "end": v(-10.05, -7.62) * mm});
            skLineSegment(sketch, "E209.right", {"start": v(28.1, -12.38) * mm, "end": v(28.1, -7.62) * mm});
            skPoint(sketch, "E209.top.end.orphan", {"position": v(28.1, -2.88) * mm});
            skLineSegment(sketch, "E210.bottom", {"start": v(186.84, -7.62) * mm, "end": v(224.98, -7.62) * mm});
            skLineSegment(sketch, "E210.left", {"start": v(186.84, -7.62) * mm, "end": v(186.84, -26.67) * mm});
            skLineSegment(sketch, "E210.right", {"start": v(224.98, -7.62) * mm, "end": v(224.98, -26.67) * mm});
            skArc(sketch, "E211", {"start": v(186.84, -26.67) * mm, "mid": v(177.9, -50) * mm, "end": v(191.03, -71.24) * mm});
            skArc(sketch, "E212", {"start": v(220.78, -71.24) * mm, "mid": v(205.9, -19.22) * mm, "end": v(191.03, -71.24) * mm});
            skArc(sketch, "E213", {"start": v(216.83, -66.7) * mm, "mid": v(205.9, -25.13) * mm, "end": v(194.98, -66.7) * mm});
            skPoint(sketch, "E214", {"position": v(194.98, -66.7) * mm});
            skPoint(sketch, "E215", {"position": v(191.03, -71.24) * mm});
            skPoint(sketch, "E216.MirrorP", {"position": v(216.83, -66.7) * mm});
            skPoint(sketch, "E217.MirrorP", {"position": v(220.78, -71.24) * mm});
            skArc(sketch, "E218.trimOffspring", {"start": v(220.78, -71.24) * mm, "mid": v(233.92, -50) * mm, "end": v(224.98, -26.67) * mm});
            skPoint(sketch, "E219.orphan", {"position": v(205.9, -7.62) * mm});
            skLineSegment(sketch, "E220", {"start": v(194.98, -66.7) * mm, "end": v(191.03, -71.24) * mm});
            skLineSegment(sketch, "E221", {"start": v(216.83, -66.7) * mm, "end": v(220.78, -71.24) * mm});
            skLineSegment(sketch, "E222.left", {"start": v(186.84, -7.62) * mm, "end": v(186.84, -17.14) * mm});
            skLineSegment(sketch, "E222.right", {"start": v(224.98, -7.62) * mm, "end": v(224.98, -17.14) * mm});
            skPoint(sketch, "E223.end.orphan", {"position": v(186.84, -12.38) * mm});
            skPoint(sketch, "E223.start.orphan", {"position": v(224.98, -12.38) * mm});
            skLineSegment(sketch, "E224.bottom", {"start": v(186.84, -12.38) * mm, "end": v(224.98, -12.38) * mm});
            skLineSegment(sketch, "E224.left", {"start": v(186.84, -12.38) * mm, "end": v(186.84, -7.62) * mm});
            skLineSegment(sketch, "E224.right", {"start": v(224.98, -12.38) * mm, "end": v(224.98, -7.62) * mm});
            skLineSegment(sketch, "E225.bottom", {"start": v(121.56, -7.62) * mm, "end": v(159.7, -7.62) * mm});
            skLineSegment(sketch, "E225.left", {"start": v(121.56, -7.62) * mm, "end": v(121.56, -26.67) * mm});
            skLineSegment(sketch, "E225.right", {"start": v(159.7, -7.62) * mm, "end": v(159.7, -26.67) * mm});
            skArc(sketch, "E226", {"start": v(121.56, -26.67) * mm, "mid": v(112.62, -50) * mm, "end": v(125.75, -71.24) * mm});
            skArc(sketch, "E227", {"start": v(155.5, -71.24) * mm, "mid": v(140.63, -19.22) * mm, "end": v(125.75, -71.24) * mm});
            skArc(sketch, "E228", {"start": v(151.56, -66.7) * mm, "mid": v(140.63, -25.13) * mm, "end": v(129.7, -66.7) * mm});
            skPoint(sketch, "E229", {"position": v(129.7, -66.7) * mm});
            skPoint(sketch, "E230", {"position": v(125.75, -71.24) * mm});
            skPoint(sketch, "E231.MirrorP", {"position": v(151.56, -66.7) * mm});
            skPoint(sketch, "E232.MirrorP", {"position": v(155.5, -71.24) * mm});
            skArc(sketch, "E233.trimOffspring", {"start": v(155.5, -71.24) * mm, "mid": v(168.64, -50) * mm, "end": v(159.7, -26.67) * mm});
            skPoint(sketch, "E234.orphan", {"position": v(140.63, -7.62) * mm});
            skLineSegment(sketch, "E235", {"start": v(129.7, -66.7) * mm, "end": v(125.75, -71.24) * mm});
            skLineSegment(sketch, "E236", {"start": v(151.56, -66.7) * mm, "end": v(155.5, -71.24) * mm});
            skLineSegment(sketch, "E237.left", {"start": v(121.56, -7.62) * mm, "end": v(121.56, -17.14) * mm});
            skLineSegment(sketch, "E237.right", {"start": v(159.7, -7.62) * mm, "end": v(159.7, -17.14) * mm});
            skPoint(sketch, "E238.end.orphan", {"position": v(121.56, -12.38) * mm});
            skPoint(sketch, "E238.start.orphan", {"position": v(159.7, -12.38) * mm});
            skLineSegment(sketch, "E239.bottom", {"start": v(121.56, -12.38) * mm, "end": v(159.7, -12.38) * mm});
            skLineSegment(sketch, "E239.left", {"start": v(121.56, -12.38) * mm, "end": v(121.56, -7.62) * mm});
            skLineSegment(sketch, "E239.right", {"start": v(159.7, -12.38) * mm, "end": v(159.7, -7.62) * mm});
            skSolve(sketch);
        }
        {
            var Q0;
            {var subQ1=sQuery(id+"F3.wireOp",EDGE,"E210.left");Q0=makeQuery(id+"F3.imprint","IMPRINT",FACE,{"disambiguationData":[TD([[makeQuery(id+"F3.imprint","IMPRINT",EDGE,{"derivedFrom":subQ1}),1.0]])]});}
            var Q1;
            Q1=makeQuery(id+"F3.imprint","IMPRINT",FACE,{"disambiguationData":[TD([[makeQuery(id+"F3.imprint","IMPRINT",EDGE,{"derivedFrom":sQuery(id+"F3.wireOp",EDGE,"E213")}),-1.0]])]});
            var Q2;
            Q2=makeQuery(id+"F3.imprint","IMPRINT",FACE,{"disambiguationData":[TD([[makeQuery(id+"F3.imprint","IMPRINT",EDGE,{"derivedFrom":sQuery(id+"F3.wireOp",EDGE,"E228")}),-1.0]])]});
            var Q3;
            {var subQ1=sQuery(id+"F3.wireOp",EDGE,"E225.left");Q3=makeQuery(id+"F3.imprint","IMPRINT",FACE,{"disambiguationData":[TD([[makeQuery(id+"F3.imprint","IMPRINT",EDGE,{"derivedFrom":subQ1}),1.0]])]});}
            var Q4;
            {var subQ1=sQuery(id+"F3.wireOp",EDGE,"E180.left");Q4=makeQuery(id+"F3.imprint","IMPRINT",FACE,{"disambiguationData":[TD([[makeQuery(id+"F3.imprint","IMPRINT",EDGE,{"derivedFrom":subQ1}),1.0]])]});}
            var Q5;
            Q5=makeQuery(id+"F3.imprint","IMPRINT",FACE,{"disambiguationData":[TD([[makeQuery(id+"F3.imprint","IMPRINT",EDGE,{"derivedFrom":sQuery(id+"F3.wireOp",EDGE,"E183")}),-1.0]])]});
            var Q6;
            {var subQ1=sQuery(id+"F3.wireOp",EDGE,"E195.left");Q6=makeQuery(id+"F3.imprint","IMPRINT",FACE,{"disambiguationData":[TD([[makeQuery(id+"F3.imprint","IMPRINT",EDGE,{"derivedFrom":subQ1}),1.0]])]});}
            var Q7;
            Q7=makeQuery(id+"F3.imprint","IMPRINT",FACE,{"disambiguationData":[TD([[makeQuery(id+"F3.imprint","IMPRINT",EDGE,{"derivedFrom":sQuery(id+"F3.wireOp",EDGE,"E198")}),-1.0]])]});
            var Q8;
            {var subQ1=sQuery(id+"F3.wireOp",EDGE,"E150.left");Q8=makeQuery(id+"F3.imprint","IMPRINT",FACE,{"disambiguationData":[TD([[makeQuery(id+"F3.imprint","IMPRINT",EDGE,{"derivedFrom":subQ1}),1.0]])]});}
            var Q9;
            Q9=makeQuery(id+"F3.imprint","IMPRINT",FACE,{"disambiguationData":[TD([[makeQuery(id+"F3.imprint","IMPRINT",EDGE,{"derivedFrom":sQuery(id+"F3.wireOp",EDGE,"E153")}),-1.0]])]});
            var Q10;
            {var subQ1=sQuery(id+"F3.wireOp",EDGE,"E165.left");Q10=makeQuery(id+"F3.imprint","IMPRINT",FACE,{"disambiguationData":[TD([[makeQuery(id+"F3.imprint","IMPRINT",EDGE,{"derivedFrom":subQ1}),1.0]])]});}
            var Q11;
            Q11=makeQuery(id+"F3.imprint","IMPRINT",FACE,{"disambiguationData":[TD([[makeQuery(id+"F3.imprint","IMPRINT",EDGE,{"derivedFrom":sQuery(id+"F3.wireOp",EDGE,"E168")}),-1.0]])]});
            var Q12;
            {var subQ1=sQuery(id+"F3.wireOp",EDGE,"E120.left");Q12=makeQuery(id+"F3.imprint","IMPRINT",FACE,{"disambiguationData":[TD([[makeQuery(id+"F3.imprint","IMPRINT",EDGE,{"derivedFrom":subQ1}),1.0]])]});}
            var Q13;
            Q13=makeQuery(id+"F3.imprint","IMPRINT",FACE,{"disambiguationData":[TD([[makeQuery(id+"F3.imprint","IMPRINT",EDGE,{"derivedFrom":sQuery(id+"F3.wireOp",EDGE,"E123")}),-1.0]])]});
            var Q14;
            {var subQ1=sQuery(id+"F3.wireOp",EDGE,"E135.left");Q14=makeQuery(id+"F3.imprint","IMPRINT",FACE,{"disambiguationData":[TD([[makeQuery(id+"F3.imprint","IMPRINT",EDGE,{"derivedFrom":subQ1}),1.0]])]});}
            var Q15;
            Q15=makeQuery(id+"F3.imprint","IMPRINT",FACE,{"disambiguationData":[TD([[makeQuery(id+"F3.imprint","IMPRINT",EDGE,{"derivedFrom":sQuery(id+"F3.wireOp",EDGE,"E138")}),-1.0]])]});
            extrude(context, id + "F4", {"entities" : qUnion([Q0, Q1, Q2, Q3, Q4, Q5, Q6, Q7, Q8, Q9, Q10, Q11, Q12, Q13, Q14, Q15]), "depth" : 25.4 * mm});
        }
        {
            var Q0;
            Q0=makeQuery(id+"F0.imprint","IMPRINT",FACE,{"disambiguationData":[TD([[makeQuery(id+"F0.imprint","IMPRINT",EDGE,{"derivedFrom":sQuery(id+"F0.wireOp",EDGE,"E15.bottom")}),-1.0]])]});
            var Q1;
            Q1=makeQuery(id+"F0.imprint","IMPRINT",FACE,{"disambiguationData":[TD([[makeQuery(id+"F0.imprint","IMPRINT",EDGE,{"derivedFrom":sQuery(id+"F0.wireOp",EDGE,"E0.bottom")}),-1.0]])]});
            var Q2;
            Q2=makeQuery(id+"F0.imprint","IMPRINT",FACE,{"disambiguationData":[TD([[makeQuery(id+"F0.imprint","IMPRINT",EDGE,{"derivedFrom":sQuery(id+"F0.wireOp",EDGE,"E45.bottom")}),-1.0]])]});
            var Q3;
            Q3=makeQuery(id+"F0.imprint","IMPRINT",FACE,{"disambiguationData":[TD([[makeQuery(id+"F0.imprint","IMPRINT",EDGE,{"derivedFrom":sQuery(id+"F0.wireOp",EDGE,"E30.bottom")}),-1.0]])]});
            var Q4;
            Q4=makeQuery(id+"F0.imprint","IMPRINT",FACE,{"disambiguationData":[TD([[makeQuery(id+"F0.imprint","IMPRINT",EDGE,{"derivedFrom":sQuery(id+"F0.wireOp",EDGE,"E75.bottom")}),-1.0]])]});
            var Q5;
            Q5=makeQuery(id+"F0.imprint","IMPRINT",FACE,{"disambiguationData":[TD([[makeQuery(id+"F0.imprint","IMPRINT",EDGE,{"derivedFrom":sQuery(id+"F0.wireOp",EDGE,"E60.bottom")}),-1.0]])]});
            var Q6;
            Q6=makeQuery(id+"F0.imprint","IMPRINT",FACE,{"disambiguationData":[TD([[makeQuery(id+"F0.imprint","IMPRINT",EDGE,{"derivedFrom":sQuery(id+"F0.wireOp",EDGE,"E105.bottom")}),-1.0]])]});
            var Q7;
            Q7=makeQuery(id+"F0.imprint","IMPRINT",FACE,{"disambiguationData":[TD([[makeQuery(id+"F0.imprint","IMPRINT",EDGE,{"derivedFrom":sQuery(id+"F0.wireOp",EDGE,"E90.bottom")}),-1.0]])]});
            var Q8;
            Q8=makeQuery(id+"F0.imprint","IMPRINT",FACE,{"disambiguationData":[TD([[makeQuery(id+"F0.imprint","IMPRINT",EDGE,{"derivedFrom":sQuery(id+"F0.wireOp",EDGE,"4435aaf2-8c3e-4714-bde2-66812a234214.bottom")}),-1.0]])]});
            extrude(context, id + "F5", {"entities" : qUnion([Q0, Q1, Q2, Q3, Q4, Q5, Q6, Q7, Q8]), "depth" : 50.8 * mm});
        }
        {
            var Q0;
            Q0=makeQuery(id+"F3.imprint","IMPRINT",FACE,{"disambiguationData":[TD([[makeQuery(id+"F3.imprint","IMPRINT",EDGE,{"derivedFrom":sQuery(id+"F3.wireOp",EDGE,"E210.bottom")}),-1.0]])]});
            var Q1;
            Q1=makeQuery(id+"F3.imprint","IMPRINT",FACE,{"disambiguationData":[TD([[makeQuery(id+"F3.imprint","IMPRINT",EDGE,{"derivedFrom":sQuery(id+"F3.wireOp",EDGE,"E225.bottom")}),-1.0]])]});
            var Q2;
            Q2=makeQuery(id+"F3.imprint","IMPRINT",FACE,{"disambiguationData":[TD([[makeQuery(id+"F3.imprint","IMPRINT",EDGE,{"derivedFrom":sQuery(id+"F3.wireOp",EDGE,"E180.bottom")}),-1.0]])]});
            var Q3;
            Q3=makeQuery(id+"F3.imprint","IMPRINT",FACE,{"disambiguationData":[TD([[makeQuery(id+"F3.imprint","IMPRINT",EDGE,{"derivedFrom":sQuery(id+"F3.wireOp",EDGE,"E195.bottom")}),-1.0]])]});
            var Q4;
            Q4=makeQuery(id+"F3.imprint","IMPRINT",FACE,{"disambiguationData":[TD([[makeQuery(id+"F3.imprint","IMPRINT",EDGE,{"derivedFrom":sQuery(id+"F3.wireOp",EDGE,"E150.bottom")}),-1.0]])]});
            var Q5;
            Q5=makeQuery(id+"F3.imprint","IMPRINT",FACE,{"disambiguationData":[TD([[makeQuery(id+"F3.imprint","IMPRINT",EDGE,{"derivedFrom":sQuery(id+"F3.wireOp",EDGE,"E165.bottom")}),-1.0]])]});
            var Q6;
            Q6=makeQuery(id+"F3.imprint","IMPRINT",FACE,{"disambiguationData":[TD([[makeQuery(id+"F3.imprint","IMPRINT",EDGE,{"derivedFrom":sQuery(id+"F3.wireOp",EDGE,"E120.bottom")}),-1.0]])]});
            var Q7;
            Q7=makeQuery(id+"F3.imprint","IMPRINT",FACE,{"disambiguationData":[TD([[makeQuery(id+"F3.imprint","IMPRINT",EDGE,{"derivedFrom":sQuery(id+"F3.wireOp",EDGE,"E135.bottom")}),-1.0]])]});
            extrude(context, id + "F6", {"entities" : qUnion([Q0, Q1, Q2, Q3, Q4, Q5, Q6, Q7]), "depth" : 50.8 * mm});
        }
        {
            var Q0;
            Q0=makeQuery(id+"F5.opExtrude","SWEPT_FACE",FACE,{"disambiguationData":[OSD([sQuery(id+"F0.wireOp",EDGE,"E59.bottom")])]});
            cPlane(context, id + "F7", {"entities" : qUnion([Q0]), "cplaneType" : CPlaneType.OFFSET, "offset" : 0 * mm, "oppositeDirection" : true, "width" : 152.4 * mm, "height" : 152.4 * mm});
        }
        {
            var Q0;
            Q0=qCreatedBy(id+"F7.planeOp",FACE);
            var sketch = newSketch(context, id + "F8", { "sketchPlane" : qUnion([Q0])});
            skPoint(sketch, "E240", {"position": v(-256.4, 41.76) * mm});
            skPoint(sketch, "E241", {"position": v(-189.62, 41.76) * mm});
            skPoint(sketch, "E242", {"position": v(-122.83, 41.76) * mm});
            skPoint(sketch, "E243", {"position": v(-57.5, 41.76) * mm});
            skPoint(sketch, "E244", {"position": v(9.28, 41.76) * mm});
            skPoint(sketch, "E245", {"position": v(73.16, 41.76) * mm});
            skPoint(sketch, "E246", {"position": v(140.92, 41.76) * mm});
            skPoint(sketch, "E247", {"position": v(206.25, 41.76) * mm});
            skSolve(sketch);
        }
        {
            var Q0;
            Q0=sQuery(id+"F8.wireOp",VERTEX,"E243");
            var Q1;
            Q1=sQuery(id+"F8.wireOp",VERTEX,"E240");
            var Q2;
            Q2=sQuery(id+"F8.wireOp",VERTEX,"E242");
            var Q3;
            Q3=sQuery(id+"F8.wireOp",VERTEX,"E241");
            var Q4;
            Q4=sQuery(id+"F8.wireOp",VERTEX,"E247");
            var Q5;
            Q5=sQuery(id+"F8.wireOp",VERTEX,"E245");
            var Q6;
            Q6=sQuery(id+"F8.wireOp",VERTEX,"E244");
            var Q7;
            Q7=sQuery(id+"F8.wireOp",VERTEX,"E246");
            var Q8;
            Q8=makeQuery(id+"F5.opExtrude","SWEPT_BODY",BODY,{"disambiguationData":[OSD([sQuery(id+"F0.wireOp",EDGE,"E45.bottom"),sQuery(id+"F0.wireOp",EDGE,"E59.bottom"),sQuery(id+"F0.wireOp",EDGE,"E59.left"),sQuery(id+"F0.wireOp",EDGE,"E59.right")])]});
            var Q9;
            Q9=makeQuery(id+"F5.opExtrude","SWEPT_BODY",BODY,{"disambiguationData":[OSD([sQuery(id+"F0.wireOp",EDGE,"E0.bottom"),sQuery(id+"F0.wireOp",EDGE,"E14.bottom"),sQuery(id+"F0.wireOp",EDGE,"E14.left"),sQuery(id+"F0.wireOp",EDGE,"E14.right")])]});
            var Q10;
            Q10=makeQuery(id+"F5.opExtrude","SWEPT_BODY",BODY,{"disambiguationData":[OSD([sQuery(id+"F0.wireOp",EDGE,"E15.bottom"),sQuery(id+"F0.wireOp",EDGE,"E29.bottom"),sQuery(id+"F0.wireOp",EDGE,"E29.left"),sQuery(id+"F0.wireOp",EDGE,"E29.right")])]});
            var Q11;
            Q11=makeQuery(id+"F5.opExtrude","SWEPT_BODY",BODY,{"disambiguationData":[OSD([sQuery(id+"F0.wireOp",EDGE,"E30.bottom"),sQuery(id+"F0.wireOp",EDGE,"E44.bottom"),sQuery(id+"F0.wireOp",EDGE,"E44.left"),sQuery(id+"F0.wireOp",EDGE,"E44.right")])]});
            var Q12;
            Q12=makeQuery(id+"F5.opExtrude","SWEPT_BODY",BODY,{"disambiguationData":[OSD([sQuery(id+"F0.wireOp",EDGE,"E75.bottom"),sQuery(id+"F0.wireOp",EDGE,"E89.bottom"),sQuery(id+"F0.wireOp",EDGE,"E89.left"),sQuery(id+"F0.wireOp",EDGE,"E89.right")])]});
            var Q13;
            Q13=makeQuery(id+"F5.opExtrude","SWEPT_BODY",BODY,{"disambiguationData":[OSD([sQuery(id+"F0.wireOp",EDGE,"E60.bottom"),sQuery(id+"F0.wireOp",EDGE,"E74.bottom"),sQuery(id+"F0.wireOp",EDGE,"E74.left"),sQuery(id+"F0.wireOp",EDGE,"E74.right")])]});
            var Q14;
            Q14=makeQuery(id+"F5.opExtrude","SWEPT_BODY",BODY,{"disambiguationData":[OSD([sQuery(id+"F0.wireOp",EDGE,"E105.bottom"),sQuery(id+"F0.wireOp",EDGE,"E119.bottom"),sQuery(id+"F0.wireOp",EDGE,"E119.left"),sQuery(id+"F0.wireOp",EDGE,"E119.right")])]});
            var Q15;
            Q15=makeQuery(id+"F5.opExtrude","SWEPT_BODY",BODY,{"disambiguationData":[OSD([sQuery(id+"F0.wireOp",EDGE,"E90.bottom"),sQuery(id+"F0.wireOp",EDGE,"E104.bottom"),sQuery(id+"F0.wireOp",EDGE,"E104.left"),sQuery(id+"F0.wireOp",EDGE,"E104.right")])]});
            hole(context, id + "F9", {"style" : HoleStyle.C_SINK, "endStyle" : HoleEndStyle.THROUGH, "holeDiameter" : 6.35 * mm, "cSinkDiameter" : 9.52 * mm, "cSinkAngle" : 90 * degree, "isTappedThrough" : true, "tappedDepth" : 12.7 * mm, "tapClearance" : 3, "locations" : qUnion([Q0, Q1, Q2, Q3, Q4, Q5, Q6, Q7]), "scope" : qUnion([Q8, Q9, Q10, Q11, Q12, Q13, Q14, Q15])});
        }
        {
            var Q0;
            Q0=makeQuery(id+"F6.opExtrude","SWEPT_FACE",FACE,{"disambiguationData":[OSD([sQuery(id+"F3.wireOp",EDGE,"E179.bottom")])]});
            cPlane(context, id + "F10", {"entities" : qUnion([Q0]), "cplaneType" : CPlaneType.OFFSET, "offset" : 0 * mm, "width" : 152.4 * mm, "height" : 152.4 * mm});
        }
        {
            var Q0;
            Q0=qCreatedBy(id+"F10.planeOp",FACE);
            var sketch = newSketch(context, id + "F11", { "sketchPlane" : qUnion([Q0])});
            skPoint(sketch, "E248", {"position": v(-255.38, -88.53) * mm});
            skPoint(sketch, "E249", {"position": v(-188.6, -88.53) * mm});
            skPoint(sketch, "E250", {"position": v(-121.8, -88.53) * mm});
            skPoint(sketch, "E251", {"position": v(-56.47, -88.53) * mm});
            skPoint(sketch, "E252", {"position": v(10.31, -88.53) * mm});
            skPoint(sketch, "E253", {"position": v(74.2, -88.53) * mm});
            skPoint(sketch, "E254", {"position": v(141.94, -88.53) * mm});
            skPoint(sketch, "E255", {"position": v(207.28, -88.53) * mm});
            skSolve(sketch);
        }
        {
            var Q0;
            Q0=sQuery(id+"F11.wireOp",VERTEX,"E248");
            var Q1;
            Q1=sQuery(id+"F11.wireOp",VERTEX,"E254");
            var Q2;
            Q2=sQuery(id+"F11.wireOp",VERTEX,"E249");
            var Q3;
            Q3=sQuery(id+"F11.wireOp",VERTEX,"E253");
            var Q4;
            Q4=sQuery(id+"F11.wireOp",VERTEX,"E255");
            var Q5;
            Q5=sQuery(id+"F11.wireOp",VERTEX,"E251");
            var Q6;
            Q6=sQuery(id+"F11.wireOp",VERTEX,"E250");
            var Q7;
            Q7=sQuery(id+"F11.wireOp",VERTEX,"E252");
            var Q8;
            Q8=makeQuery(id+"F6.opExtrude","SWEPT_BODY",BODY,{"disambiguationData":[OSD([sQuery(id+"F3.wireOp",EDGE,"E120.bottom"),sQuery(id+"F3.wireOp",EDGE,"E134.bottom"),sQuery(id+"F3.wireOp",EDGE,"E134.left"),sQuery(id+"F3.wireOp",EDGE,"E134.right")])]});
            var Q9;
            Q9=makeQuery(id+"F6.opExtrude","SWEPT_BODY",BODY,{"disambiguationData":[OSD([sQuery(id+"F3.wireOp",EDGE,"E135.bottom"),sQuery(id+"F3.wireOp",EDGE,"E149.bottom"),sQuery(id+"F3.wireOp",EDGE,"E149.left"),sQuery(id+"F3.wireOp",EDGE,"E149.right")])]});
            var Q10;
            Q10=makeQuery(id+"F6.opExtrude","SWEPT_BODY",BODY,{"disambiguationData":[OSD([sQuery(id+"F3.wireOp",EDGE,"E150.bottom"),sQuery(id+"F3.wireOp",EDGE,"E164.bottom"),sQuery(id+"F3.wireOp",EDGE,"E164.left"),sQuery(id+"F3.wireOp",EDGE,"E164.right")])]});
            var Q11;
            Q11=makeQuery(id+"F6.opExtrude","SWEPT_BODY",BODY,{"disambiguationData":[OSD([sQuery(id+"F3.wireOp",EDGE,"E165.bottom"),sQuery(id+"F3.wireOp",EDGE,"E179.bottom"),sQuery(id+"F3.wireOp",EDGE,"E179.left"),sQuery(id+"F3.wireOp",EDGE,"E179.right")])]});
            var Q12;
            Q12=makeQuery(id+"F6.opExtrude","SWEPT_BODY",BODY,{"disambiguationData":[OSD([sQuery(id+"F3.wireOp",EDGE,"E180.bottom"),sQuery(id+"F3.wireOp",EDGE,"E194.bottom"),sQuery(id+"F3.wireOp",EDGE,"E194.left"),sQuery(id+"F3.wireOp",EDGE,"E194.right")])]});
            var Q13;
            Q13=makeQuery(id+"F6.opExtrude","SWEPT_BODY",BODY,{"disambiguationData":[OSD([sQuery(id+"F3.wireOp",EDGE,"E195.bottom"),sQuery(id+"F3.wireOp",EDGE,"E209.bottom"),sQuery(id+"F3.wireOp",EDGE,"E209.left"),sQuery(id+"F3.wireOp",EDGE,"E209.right")])]});
            var Q14;
            Q14=makeQuery(id+"F6.opExtrude","SWEPT_BODY",BODY,{"disambiguationData":[OSD([sQuery(id+"F3.wireOp",EDGE,"E210.bottom"),sQuery(id+"F3.wireOp",EDGE,"E224.bottom"),sQuery(id+"F3.wireOp",EDGE,"E224.left"),sQuery(id+"F3.wireOp",EDGE,"E224.right")])]});
            var Q15;
            Q15=makeQuery(id+"F6.opExtrude","SWEPT_BODY",BODY,{"disambiguationData":[OSD([sQuery(id+"F3.wireOp",EDGE,"E225.bottom"),sQuery(id+"F3.wireOp",EDGE,"E239.bottom"),sQuery(id+"F3.wireOp",EDGE,"E239.left"),sQuery(id+"F3.wireOp",EDGE,"E239.right")])]});
            hole(context, id + "F12", {"style" : HoleStyle.C_SINK, "endStyle" : HoleEndStyle.THROUGH, "holeDiameter" : 6.35 * mm, "cSinkDiameter" : 9.52 * mm, "cSinkAngle" : 90 * degree, "isTappedThrough" : true, "tappedDepth" : 12.7 * mm, "tapClearance" : 3, "locations" : qUnion([Q0, Q1, Q2, Q3, Q4, Q5, Q6, Q7]), "scope" : qUnion([Q8, Q9, Q10, Q11, Q12, Q13, Q14, Q15])});
        }
        {
            var Q0;
            Q0=makeQuery(id+"F1.opExtrude","CAP_EDGE",EDGE,{"disambiguationData":[OSD([sQuery(id+"F0.wireOp",EDGE,"E18")])],"isStart":false});
            var Q1;
            Q1=makeQuery(id+"F1.opExtrude","CAP_EDGE",EDGE,{"disambiguationData":[OSD([sQuery(id+"F0.wireOp",EDGE,"E3")])],"isStart":false});
            var Q2;
            Q2=makeQuery(id+"F1.opExtrude","CAP_EDGE",EDGE,{"disambiguationData":[OSD([sQuery(id+"F0.wireOp",EDGE,"E48")])],"isStart":false});
            var Q3;
            Q3=makeQuery(id+"F1.opExtrude","CAP_EDGE",EDGE,{"disambiguationData":[OSD([sQuery(id+"F0.wireOp",EDGE,"E33")])],"isStart":false});
            var Q4;
            Q4=makeQuery(id+"F1.opExtrude","CAP_EDGE",EDGE,{"disambiguationData":[OSD([sQuery(id+"F0.wireOp",EDGE,"E78")])],"isStart":false});
            var Q5;
            Q5=makeQuery(id+"F1.opExtrude","CAP_EDGE",EDGE,{"disambiguationData":[OSD([sQuery(id+"F0.wireOp",EDGE,"E63")])],"isStart":false});
            var Q6;
            Q6=makeQuery(id+"F1.opExtrude","CAP_EDGE",EDGE,{"disambiguationData":[OSD([sQuery(id+"F0.wireOp",EDGE,"E108")])],"isStart":false});
            var Q7;
            Q7=makeQuery(id+"F1.opExtrude","CAP_EDGE",EDGE,{"disambiguationData":[OSD([sQuery(id+"F0.wireOp",EDGE,"E93")])],"isStart":false});
            var Q8;
            Q8=makeQuery(id+"F4.opExtrude","CAP_EDGE",EDGE,{"disambiguationData":[OSD([sQuery(id+"F3.wireOp",EDGE,"E213")])],"isStart":false});
            var Q9;
            Q9=makeQuery(id+"F4.opExtrude","CAP_EDGE",EDGE,{"disambiguationData":[OSD([sQuery(id+"F3.wireOp",EDGE,"E228")])],"isStart":false});
            var Q10;
            Q10=makeQuery(id+"F4.opExtrude","CAP_EDGE",EDGE,{"disambiguationData":[OSD([sQuery(id+"F3.wireOp",EDGE,"E183")])],"isStart":false});
            var Q11;
            Q11=makeQuery(id+"F4.opExtrude","CAP_EDGE",EDGE,{"disambiguationData":[OSD([sQuery(id+"F3.wireOp",EDGE,"E198")])],"isStart":false});
            var Q12;
            Q12=makeQuery(id+"F4.opExtrude","CAP_EDGE",EDGE,{"disambiguationData":[OSD([sQuery(id+"F3.wireOp",EDGE,"E153")])],"isStart":false});
            var Q13;
            Q13=makeQuery(id+"F4.opExtrude","CAP_EDGE",EDGE,{"disambiguationData":[OSD([sQuery(id+"F3.wireOp",EDGE,"E168")])],"isStart":false});
            var Q14;
            Q14=makeQuery(id+"F4.opExtrude","CAP_EDGE",EDGE,{"disambiguationData":[OSD([sQuery(id+"F3.wireOp",EDGE,"E123")])],"isStart":false});
            var Q15;
            Q15=makeQuery(id+"F4.opExtrude","CAP_EDGE",EDGE,{"disambiguationData":[OSD([sQuery(id+"F3.wireOp",EDGE,"E138")])],"isStart":false});
            var Q16;
            Q16=makeQuery(id+"F1.opExtrude","CAP_EDGE",EDGE,{"disambiguationData":[OSD([sQuery(id+"F0.wireOp",EDGE,"c035edba-2ca9-43be-b41b-8822a2fe950e")])],"isStart":false});
            fillet(context, id + "F13", {"entities" : qUnion([Q0, Q1, Q2, Q3, Q4, Q5, Q6, Q7, Q8, Q9, Q10, Q11, Q12, Q13, Q14, Q15, Q16]), "radius" : 5.08 * mm, "tangentPropagation" : true, "allowEdgeOverflow" : false});
        }
        {
            var Q0;
            Q0=makeQuery(id+"F5.opExtrude","SWEPT_FACE",FACE,{"disambiguationData":[OSD([sQuery(id+"F0.wireOp",EDGE,"E30.bottom")])]});
            cPlane(context, id + "F14", {"entities" : qUnion([Q0]), "cplaneType" : CPlaneType.OFFSET, "offset" : 0 * mm, "oppositeDirection" : true, "width" : 152.4 * mm, "height" : 152.4 * mm});
        }
        {
            var Q0;
            Q0=qCreatedBy(id+"F14.planeOp",FACE);
            var sketch = newSketch(context, id + "F15", { "sketchPlane" : qUnion([Q0])});
            skLineSegment(sketch, "E256.bottom", {"start": v(-255.6, 82.32) * mm, "end": v(312.9, 82.32) * mm});
            skLineSegment(sketch, "E256.top", {"start": v(-255.6, -159.39) * mm, "end": v(312.9, -159.39) * mm});
            skLineSegment(sketch, "E256.left", {"start": v(-255.6, 82.32) * mm, "end": v(-255.6, -159.39) * mm});
            skLineSegment(sketch, "E256.right", {"start": v(312.9, 82.32) * mm, "end": v(312.9, -159.39) * mm});
            skSolve(sketch);
        }
        {
            var Q0;
            Q0=makeQuery(id+"F15.imprint","IMPRINT",FACE,{"disambiguationData":[TD([[makeQuery(id+"F15.imprint","IMPRINT",EDGE,{"derivedFrom":sQuery(id+"F15.wireOp",EDGE,"E256.bottom")}),-1.0]])]});
            extrude(context, id + "F16", {"entities" : qUnion([Q0]), "depth" : 25.4 * mm});
        }
        {
            var Q0;
            Q0=makeQuery(id+"F16.opExtrude","CAP_FACE",FACE,{"disambiguationData":[OSD([sQuery(id+"F15.wireOp",EDGE,"E256.bottom"),sQuery(id+"F15.wireOp",EDGE,"E256.top"),sQuery(id+"F15.wireOp",EDGE,"E256.left"),sQuery(id+"F15.wireOp",EDGE,"E256.right")])],"isStart":true});
            var sketch = newSketch(context, id + "F17", { "sketchPlane" : qUnion([Q0])});
            skPoint(sketch, "E257", {"position": v(-293.05, 63.37) * mm});
            skPoint(sketch, "E258", {"position": v(235.11, 63.37) * mm});
            skSolve(sketch);
        }
        {
            var Q0;
            Q0=sQuery(id+"F17.wireOp",VERTEX,"E257");
            var Q1;
            Q1=sQuery(id+"F17.wireOp",VERTEX,"E258");
            var Q2;
            Q2=makeQuery(id+"F16.opExtrude","SWEPT_BODY",BODY,{"disambiguationData":[OSD([sQuery(id+"F15.wireOp",EDGE,"E256.bottom"),sQuery(id+"F15.wireOp",EDGE,"E256.top"),sQuery(id+"F15.wireOp",EDGE,"E256.left"),sQuery(id+"F15.wireOp",EDGE,"E256.right")])]});
            hole(context, id + "F18", {"style" : HoleStyle.C_SINK, "endStyle" : HoleEndStyle.THROUGH, "holeDiameter" : 6.35 * mm, "cSinkDiameter" : 9.52 * mm, "cSinkAngle" : 90 * degree, "isTappedThrough" : true, "tappedDepth" : 12.7 * mm, "tapClearance" : 3, "locations" : qUnion([Q0, Q1]), "scope" : qUnion([Q2])});
        }
    });
